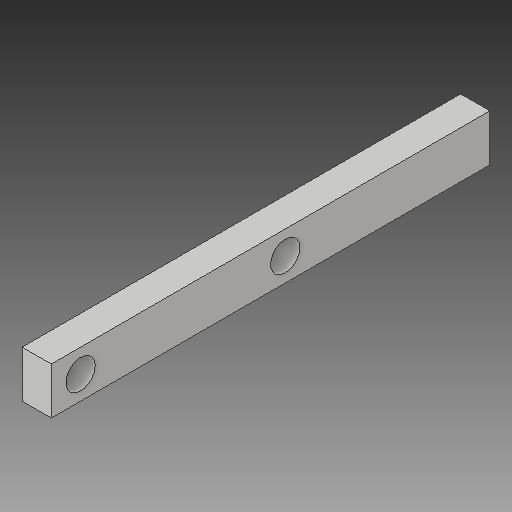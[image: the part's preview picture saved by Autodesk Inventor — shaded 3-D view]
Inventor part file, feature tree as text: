
AUTODESK INVENTOR PART (.ipt)
format: ipt  version: 2019 (Build 230136000, 136)  size: 104,448 bytes
history: native  units: mm
features: sketch x3, hole x2, extrude x1
ambient origin geometry x8: Origin, YZ Plane, XZ Plane, XY Plane, X Axis, Y Axis, Z Axis, Center Point
bodies: Solid1 (feature_tree)
feature tree (6):
  extrude  "Extrusion1"  Depth=16.0mm
  hole  "Hole1"  [1 undecoded]
  hole  "Hole2"  [1 undecoded]
  sketch  "Sketch1"  dims[d0=16.0mm d1=8.0mm]
  sketch  "Sketch2"  dims[d2=10.0mm d3=150.0mm]
  sketch  "Sketch3"  dims[d4=10.0mm d5=0.0mm d6=10.0mm d7=6.0mm d8=22.0mm d9=10.0mm d10=90.0deg d11=22.0mm d12=20.594885mm d13=10.0mm d14=6.0mm d15=22.0mm d16=10.0mm d17=90.0deg d18=22.0mm d19=20.594885mm d20=0.0mm d21=70.0mm]
note: 2 required parameter values undecoded (feature->parameter linkage not recoverable at this tier; creation-order binding heuristic only, values carry confidence <= 0.55)
